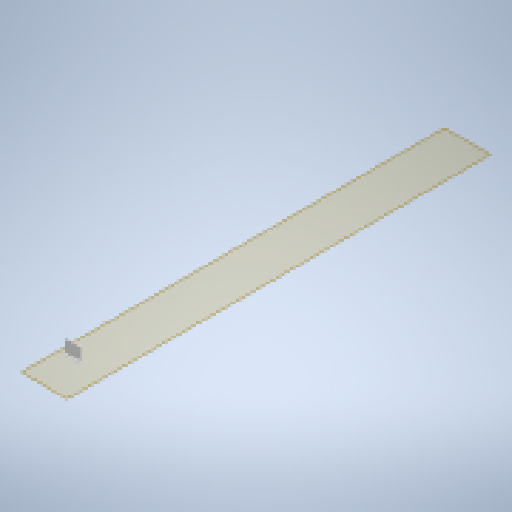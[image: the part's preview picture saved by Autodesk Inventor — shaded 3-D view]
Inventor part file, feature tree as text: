
AUTODESK INVENTOR PART (.ipt)
format: ipt  version: 2023 (Build 270158000, 158)  size: 183,296 bytes
history: native  units: mm
features: other x4, extrude x3, reference x3, sketch x2, plane x1
ambient origin geometry x8: Origin, YZ Plane, XZ Plane, XY Plane, X Axis, Y Axis, Z Axis, Center Point
bodies: Solid1 (feature_tree)
feature tree (13):
  plane  "Work Plane1"
  extrude  "Extrusion1"  Depth=50.0mm TaperAngle=0.0deg
  sketch  "Sketch2"  dims[d3=3.0mm d4=7.0mm d5=0.0mm d6=64.0mm d7=37.5mm d8=32.0mm d9=7.85mm d10=2.0mm d11=7.15mm d12=0.0mm d13=50.0mm d14=40.0mm]
  extrude  "Extrusion2"  Depth=7.0mm TaperAngle=0.0deg
  extrude  "Extrusion3"  Depth=50.0mm
  sketch  "Sketch1"  dims[d0=2.0mm d1=50.0mm d2=0.0mm]
  reference  "Reference1"
  reference  "Reference2"
  reference  "Reference3"
  parser-record x1  (decoder bookkeeping rows leaked as tree rows — omitted from the tree; the rows remain in map.json)
  other  "doorLockAssembly_V4.iam"
  other  "moulding:1"
  other  "gear_V4:1"
note: 1 file-system path scrubbed to <path> (originals preserved in map.json)
